# Revit family: Keilhauer_Juxta_Bar_Counter_Stools
name_source: partatom
category: Furniture
units: mm (PartAtom-declared; Revit-internal decimal feet)

## family parameters
Always vertical = Yes
Cut with Voids When Loaded = No
OmniClass Number = 23.40.70.14.64.11
OmniClass Title = Office Furniture
Room Calculation Point = No
Shared = No
Work Plane-Based = No

## types (6) — shared parameters
Assembly Code = E2020200
Catalog = JUXTA
Manufacturer = Keilhauer, Corp.
Product Documentation Link = http://www.keilhauer.com
URL = http://www.keilhauer.com
zero-valued in all types: Default Elevation

## per-type parameters (varying)
| type | B | Back | Backless | C | Cylinder Height | Five Star | Four Star | Four_Star_2D_Back | Four_Star_2D_Backless | Model |
| Counter Stool Low Back 4 Star Base | No | Yes | No | Yes | 21.63 " | No | Yes | Yes | No | 46642 |
| Bar Stool Low Back 4 Star Base | Yes | Yes | No | No | 26.3 " | No | Yes | Yes | No | 46643 |
| Counter Stool Low Back 5 Star Base | No | Yes | No | Yes | 21.63 " | Yes | No | No | No | 46652 |
| Bar Stool Low Back 5 Star Base | Yes | Yes | No | No | 26.3 " | Yes | No | No | No | 46653 |
| Bar Stool Backless 4 Star Base | Yes | No | Yes | No | 26.3 " | No | Yes | No | Yes | 46743 |
| Counter Stool Backless 4 Star Base | No | No | Yes | Yes | 21.63 " | No | Yes | No | Yes | 46742 |

note: column(s) folded — value = type name in every type: Description

## geometry (parser evidence)
native form markers: Sweep x2
no freeform markers — native parametric forms only
